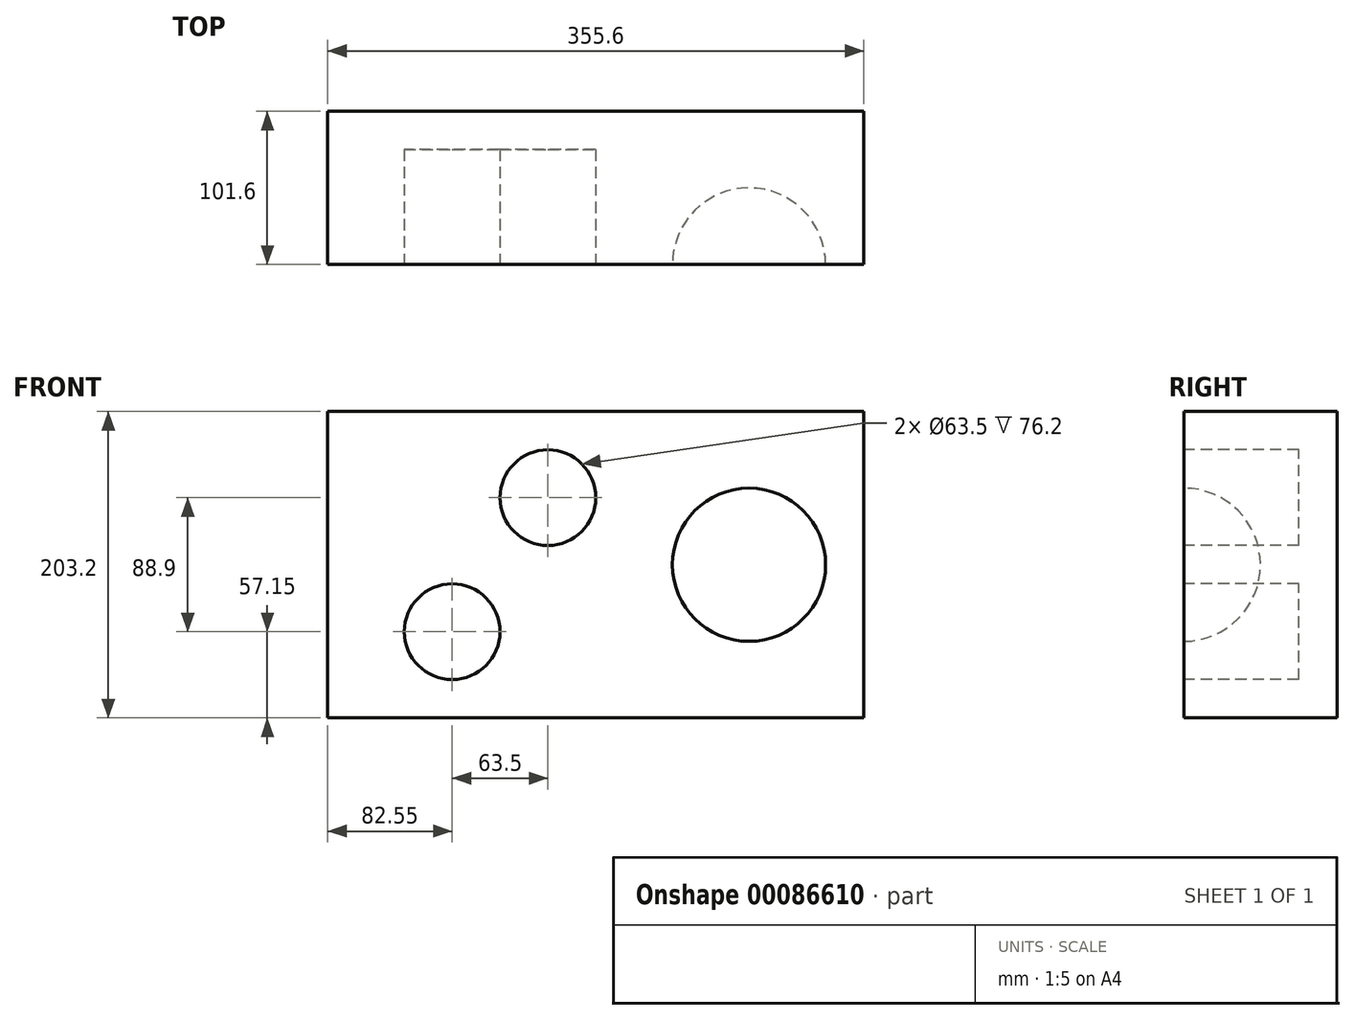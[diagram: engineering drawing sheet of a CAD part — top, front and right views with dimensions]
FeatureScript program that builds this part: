
annotation { "Feature Type Name" : "Feature", "Feature Type Description" : "" }
export const myFeature = defineFeature(function(context is Context, id is Id, definition is map)
    precondition{}
    {
        {
            var Q0;
            Q0=qCreatedBy(makeId("Front.planeOp"),FACE);
            var sketch = newSketch(context, id + "F0", { "sketchPlane" : qUnion([Q0])});
            skLineSegment(sketch, "E0.bottom", {"start": v(177.8, 101.6) * mm, "end": v(-177.8, 101.6) * mm});
            skLineSegment(sketch, "E0.top", {"start": v(177.8, -101.6) * mm, "end": v(-177.8, -101.6) * mm});
            skLineSegment(sketch, "E0.left", {"start": v(177.8, 101.6) * mm, "end": v(177.8, -101.6) * mm});
            skLineSegment(sketch, "E0.right", {"start": v(-177.8, 101.6) * mm, "end": v(-177.8, -101.6) * mm});
            skPoint(sketch, "E0.middle", {"position": v(0, 0) * mm});
            skArc(sketch, "E1", {"start": v(101.6, -50.8) * mm, "mid": v(152.4, 0) * mm, "end": v(101.6, 50.8) * mm});
            skLineSegment(sketch, "E2", {"start": v(101.6, 0) * mm, "end": v(101.6, -50.8) * mm});
            skLineSegment(sketch, "E3", {"start": v(101.6, -50.8) * mm, "end": v(101.6, 50.8) * mm});
            skCircle(sketch, "E4", {"center": v(-31.75, 44.45) * mm, "radius": 31.75 * mm});
            skCircle(sketch, "E5", {"center": v(-95.25, -44.45) * mm, "radius": 31.75 * mm});
            skSolve(sketch);
        }
        {
            var Q0;
            Q0=makeQuery(id+"F0.imprint","IMPRINT",FACE,{"disambiguationData":[TD([[makeQuery(id+"F0.imprint","IMPRINT",EDGE,{"derivedFrom":sQuery(id+"F0.wireOp",EDGE,"E0.bottom")}),1.0]])]});
            var Q1;
            {var subQ0=sQuery(id+"F0.wireOp",EDGE,"E1");Q1=makeQuery(id+"F0.imprint","IMPRINT",FACE,{"disambiguationData":[TD([[makeQuery(id+"F0.imprint","IMPRINT",EDGE,{"derivedFrom":subQ0}),1.0]])]});}
            var Q2;
            Q2=makeQuery(id+"F0.imprint","IMPRINT",FACE,{"disambiguationData":[TD([[makeQuery(id+"F0.imprint","IMPRINT",EDGE,{"derivedFrom":sQuery(id+"F0.wireOp",EDGE,"E4")}),1.0]])]});
            var Q3;
            Q3=makeQuery(id+"F0.imprint","IMPRINT",FACE,{"disambiguationData":[TD([[makeQuery(id+"F0.imprint","IMPRINT",EDGE,{"derivedFrom":sQuery(id+"F0.wireOp",EDGE,"E5")}),1.0]])]});
            extrude(context, id + "F1", {"entities" : qUnion([Q0, Q1, Q2, Q3]), "oppositeDirection" : true, "depth" : 101.6 * mm});
        }
        {
            var Q0;
            {var subQ0=sQuery(id+"F0.wireOp",EDGE,"E1");Q0=makeQuery(id+"F0.imprint","IMPRINT",FACE,{"disambiguationData":[TD([[makeQuery(id+"F0.imprint","IMPRINT",EDGE,{"derivedFrom":subQ0}),1.0]])]});}
            var Q1;
            Q1=sQuery(id+"F0.wireOp",EDGE,"E3");
            revolve(context, id + "F2", {"operationType" : NewBodyOperationType.REMOVE, "entities" : qUnion([Q0]), "axis" : qUnion([Q1]), "revolveType" : RevolveType.FULL, "oppositeDirection" : true});
        }
        {
            var Q0;
            Q0=makeQuery(id+"F0.imprint","IMPRINT",FACE,{"disambiguationData":[TD([[makeQuery(id+"F0.imprint","IMPRINT",EDGE,{"derivedFrom":sQuery(id+"F0.wireOp",EDGE,"E4")}),1.0]])]});
            var Q1;
            Q1=makeQuery(id+"F0.imprint","IMPRINT",FACE,{"disambiguationData":[TD([[makeQuery(id+"F0.imprint","IMPRINT",EDGE,{"derivedFrom":sQuery(id+"F0.wireOp",EDGE,"E5")}),1.0]])]});
            extrude(context, id + "F3", {"entities" : qUnion([Q0, Q1]), "operationType" : NewBodyOperationType.REMOVE, "oppositeDirection" : true, "depth" : 76.2 * mm});
        }
    });
